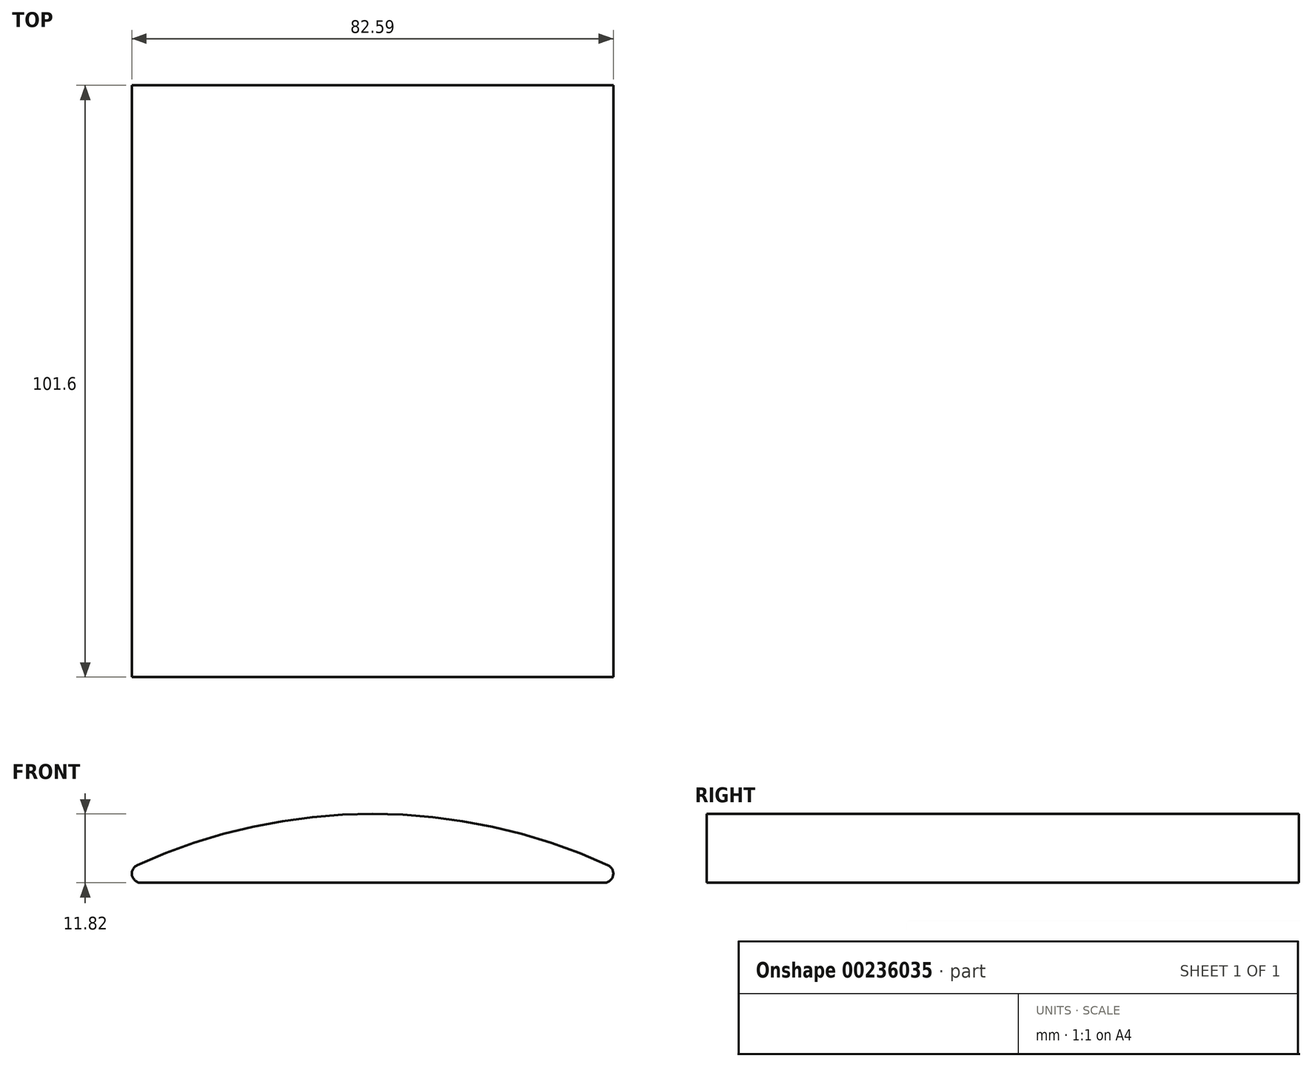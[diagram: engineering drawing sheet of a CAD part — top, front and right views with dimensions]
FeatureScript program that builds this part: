
annotation { "Feature Type Name" : "Feature", "Feature Type Description" : "" }
export const myFeature = defineFeature(function(context is Context, id is Id, definition is map)
    precondition{}
    {
        {
            var Q0;
            Q0=qCreatedBy(makeId("Front.planeOp"),FACE);
            var sketch = newSketch(context, id + "F0", { "sketchPlane" : qUnion([Q0])});
            skLineSegment(sketch, "E0", {"start": v(-45.29, 0) * mm, "end": v(47.58, 0) * mm});
            skArc(sketch, "E1", {"start": v(47.58, 0) * mm, "mid": v(1.14, 11.82) * mm, "end": v(-45.29, 0) * mm});
            skSolve(sketch);
        }
        {
            var Q0;
            Q0=makeQuery(id+"F0.imprint","IMPRINT",FACE,{"disambiguationData":[TD([[makeQuery(id+"F0.imprint","IMPRINT",EDGE,{"derivedFrom":sQuery(id+"F0.wireOp",EDGE,"E0")}),1.0]])]});
            var Q1;
            Q1=sQuery(id+"F0.wireOp",EDGE,"E1");
            extrude(context, id + "F1", {"entities" : qUnion([Q0]), "surfaceEntities" : qUnion([Q1]), "oppositeDirection" : true, "depth" : 101.6 * mm});
        }
        {
            var Q0;
            {var subQ0=sQuery(id+"F0.wireOp",EDGE,"E1");var subQ1=sQuery(id+"F0.wireOp",EDGE,"E0");Q0=makeQuery(id+"F1.opExtrude","SWEPT_EDGE",EDGE,{"disambiguationData":[OSD([subQ1,subQ0]),TDD([makeQuery(id+"F0.imprint","INTERSECT",VERTEX,{"disambiguationData":[OD(1.0)],"derivedFrom":[subQ1,subQ0]})])]});}
            var Q1;
            {var subQ0=sQuery(id+"F0.wireOp",EDGE,"E1");var subQ1=sQuery(id+"F0.wireOp",EDGE,"E0");Q1=makeQuery(id+"F1.opExtrude","SWEPT_EDGE",EDGE,{"disambiguationData":[OSD([subQ1,subQ0]),TDD([makeQuery(id+"F0.imprint","INTERSECT",VERTEX,{"disambiguationData":[OD(0.0)],"derivedFrom":[subQ1,subQ0]})])]});}
            fillet(context, id + "F2", {"entities" : qUnion([Q0, Q1]), "radius" : 1.59 * mm, "tangentPropagation" : true, "allowEdgeOverflow" : false});
        }
    });
